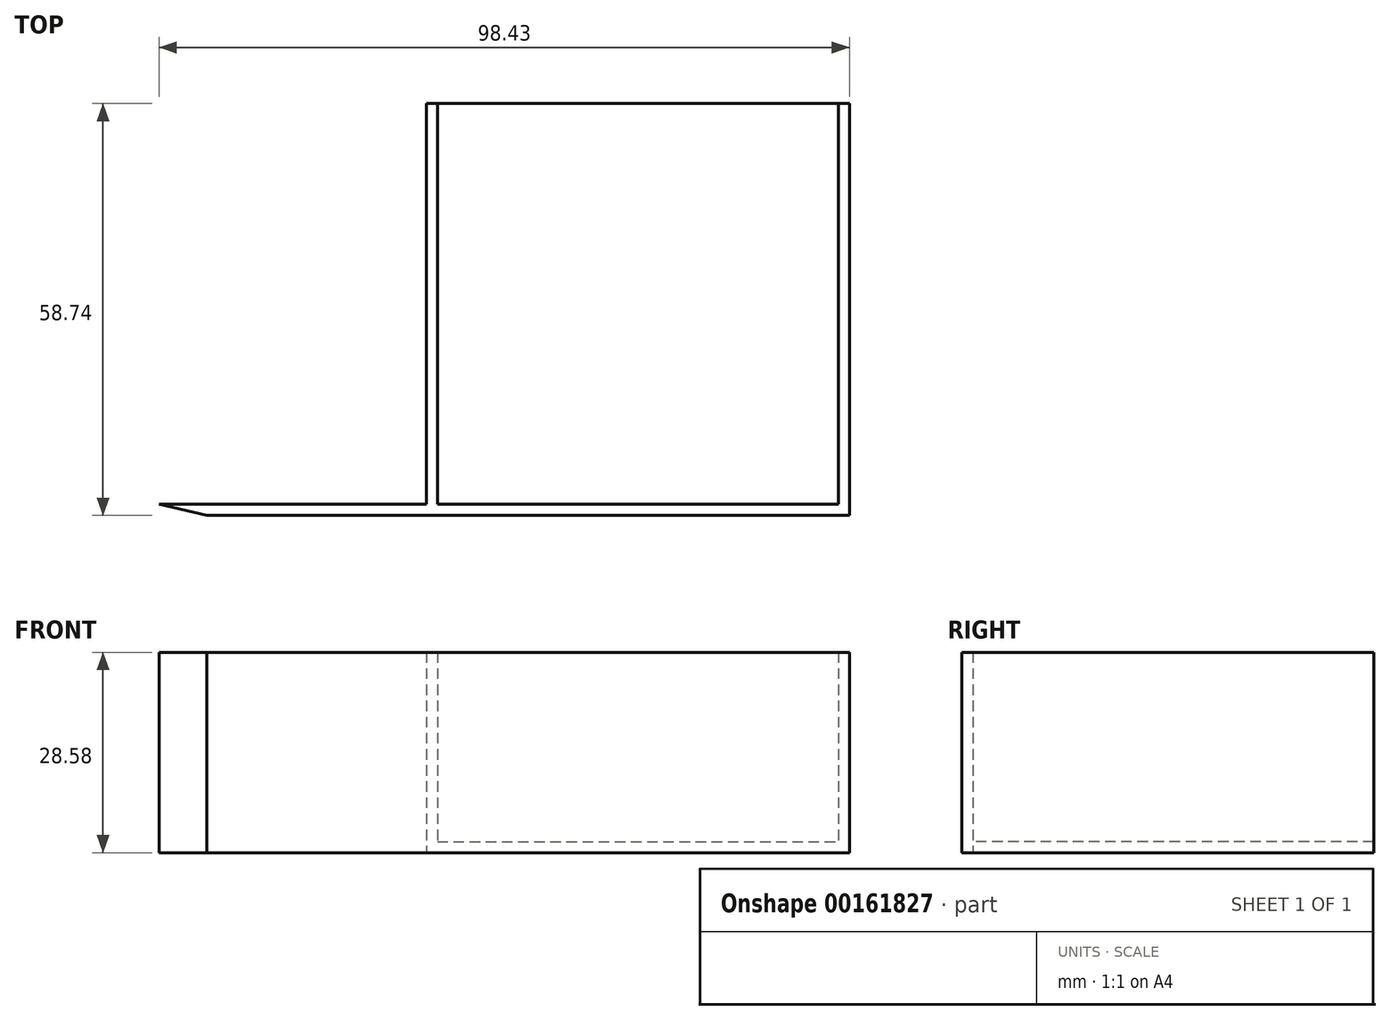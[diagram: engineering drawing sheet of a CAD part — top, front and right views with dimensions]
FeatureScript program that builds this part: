
annotation { "Feature Type Name" : "Feature", "Feature Type Description" : "" }
export const myFeature = defineFeature(function(context is Context, id is Id, definition is map)
    precondition{}
    {
        {
            var Q0;
            Q0=qCreatedBy(makeId("Top.planeOp"),FACE);
            var sketch = newSketch(context, id + "F0", { "sketchPlane" : qUnion([Q0])});
            skLineSegment(sketch, "E0", {"start": v(0, 0) * mm, "end": v(38.1, 0) * mm});
            skLineSegment(sketch, "E1", {"start": v(38.1, 0) * mm, "end": v(38.1, 57.15) * mm});
            skLineSegment(sketch, "E2", {"start": v(38.1, 57.15) * mm, "end": v(39.69, 57.15) * mm});
            skLineSegment(sketch, "E3", {"start": v(6.82, -1.59) * mm, "end": v(98.42, -1.59) * mm});
            skLineSegment(sketch, "E4", {"start": v(98.42, -1.59) * mm, "end": v(98.42, 57.15) * mm});
            skLineSegment(sketch, "E5", {"start": v(98.43, 57.15) * mm, "end": v(96.84, 57.15) * mm});
            skLineSegment(sketch, "E6", {"start": v(39.69, 57.15) * mm, "end": v(39.69, 0) * mm});
            skLineSegment(sketch, "E7", {"start": v(39.69, 0) * mm, "end": v(96.84, 0) * mm});
            skLineSegment(sketch, "E8", {"start": v(96.84, 0) * mm, "end": v(96.84, 57.15) * mm});
            skLineSegment(sketch, "E9", {"start": v(0, 0) * mm, "end": v(6.82, -1.59) * mm});
            skSolve(sketch);
        }
        {
            var Q0;
            Q0=qSketchRegion(id+"F0",true);
            extrude(context, id + "F1", {"entities" : qUnion([Q0]), "depth" : 28.57 * mm});
        }
        {
            var Q0;
            Q0=qCreatedBy(makeId("Top.planeOp"),FACE);
            var sketch = newSketch(context, id + "F2", { "sketchPlane" : qUnion([Q0])});
            skLineSegment(sketch, "E10.bottom", {"start": v(38.73, -0.82) * mm, "end": v(97.44, -0.82) * mm});
            skLineSegment(sketch, "E10.top", {"start": v(38.73, 57.15) * mm, "end": v(97.44, 57.15) * mm});
            skLineSegment(sketch, "E10.left", {"start": v(38.73, -0.82) * mm, "end": v(38.73, 57.15) * mm});
            skLineSegment(sketch, "E10.right", {"start": v(97.44, -0.82) * mm, "end": v(97.44, 57.15) * mm});
            skSolve(sketch);
        }
        {
            var Q0;
            Q0 = qSketchRegion(id + "F2", true);
            extrude(context, id + "F3", {"entities" : qUnion([Q0]), "operationType" : NewBodyOperationType.ADD, "depth" : 1.59 * mm});
        }
    });
